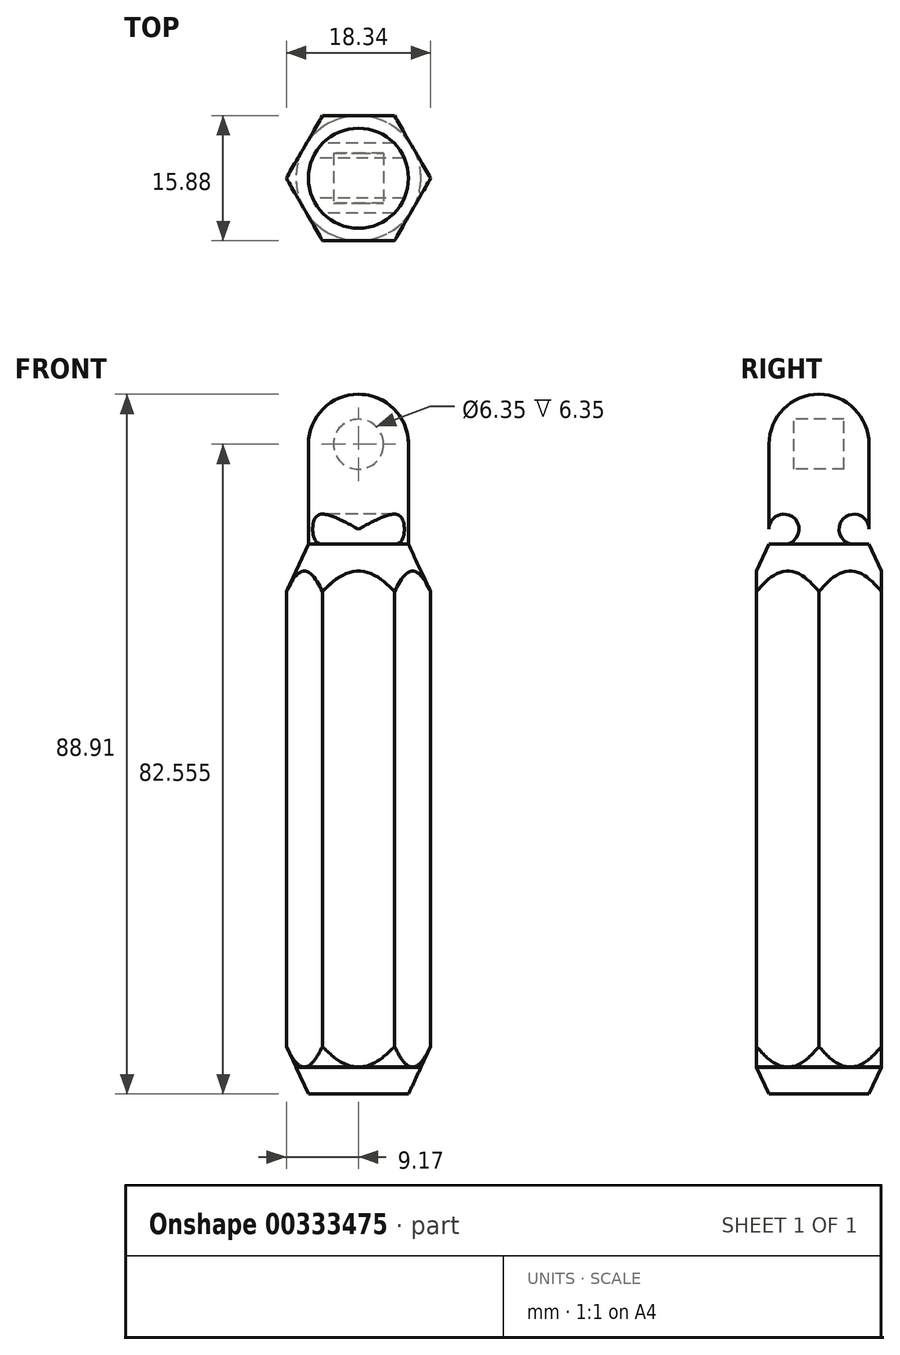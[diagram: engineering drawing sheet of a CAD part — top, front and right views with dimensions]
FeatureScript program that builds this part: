
annotation { "Feature Type Name" : "Feature", "Feature Type Description" : "" }
export const myFeature = defineFeature(function(context is Context, id is Id, definition is map)
    precondition{}
    {
        {
            var Q0;
            Q0=qCreatedBy(makeId("Front.planeOp"),FACE);
            var sketch = newSketch(context, id + "F0", { "sketchPlane" : qUnion([Q0])});
            skLineSegment(sketch, "E0.bottom", {"start": v(6.35, -34.93) * mm, "end": v(-6.35, -34.93) * mm});
            skLineSegment(sketch, "E0.top", {"start": v(6.35, 34.93) * mm, "end": v(-6.35, 34.93) * mm});
            skLineSegment(sketch, "E0.left", {"start": v(7.94, -31.52) * mm, "end": v(7.94, 31.52) * mm});
            skLineSegment(sketch, "E0.right", {"start": v(-7.94, -31.52) * mm, "end": v(-7.94, 31.52) * mm});
            skPoint(sketch, "E0.middle", {"position": v(0, 0) * mm});
            skLineSegment(sketch, "E1.left", {"start": v(6.35, 34.93) * mm, "end": v(6.35, 47.63) * mm});
            skLineSegment(sketch, "E1.right", {"start": v(-6.35, 34.93) * mm, "end": v(-6.35, 47.63) * mm});
            skArc(sketch, "E2", {"start": v(6.35, 47.63) * mm, "mid": v(0, 53.98) * mm, "end": v(-6.35, 47.63) * mm});
            skCircle(sketch, "E3", {"center": v(0, 47.63) * mm, "radius": 3.18 * mm});
            skLineSegment(sketch, "E4", {"start": v(-6.35, 34.92) * mm, "end": v(-7.94, 31.52) * mm});
            skLineSegment(sketch, "E5", {"start": v(6.35, 34.92) * mm, "end": v(7.94, 31.52) * mm});
            skPoint(sketch, "E6.orphan", {"position": v(-7.94, 34.93) * mm});
            skPoint(sketch, "E7.orphan", {"position": v(7.94, 34.93) * mm});
            skPoint(sketch, "E8.orphan", {"position": v(-6.35, 53.98) * mm});
            skPoint(sketch, "E9.orphan", {"position": v(6.35, 53.98) * mm});
            skLineSegment(sketch, "E10", {"start": v(-7.94, -31.52) * mm, "end": v(-6.35, -34.93) * mm});
            skLineSegment(sketch, "E11", {"start": v(7.94, -31.52) * mm, "end": v(6.35, -34.93) * mm});
            skPoint(sketch, "E12.orphan", {"position": v(-7.94, -34.93) * mm});
            skPoint(sketch, "E13.orphan", {"position": v(7.94, -34.93) * mm});
            skLineSegment(sketch, "E14", {"start": v(-7.94, 31.52) * mm, "end": v(7.94, 31.52) * mm});
            skLineSegment(sketch, "E15", {"start": v(0, -34.93) * mm, "end": v(0, 53.98) * mm});
            skLineSegment(sketch, "E16", {"start": v(-6.35, 34.93) * mm, "end": v(-6.35, 31.52) * mm});
            skLineSegment(sketch, "E17", {"start": v(6.35, 34.93) * mm, "end": v(6.35, 31.52) * mm});
            skLineSegment(sketch, "E18", {"start": v(-6.35, 34.93) * mm, "end": v(-12.7, 34.93) * mm});
            skLineSegment(sketch, "E19", {"start": v(-12.7, 34.92) * mm, "end": v(-12.7, 21.3) * mm});
            skLineSegment(sketch, "E20", {"start": v(-12.7, 21.3) * mm, "end": v(-6.35, 34.93) * mm});
            skLineSegment(sketch, "E21", {"start": v(6.35, 34.93) * mm, "end": v(12.7, 34.93) * mm});
            skLineSegment(sketch, "E22", {"start": v(12.7, 34.92) * mm, "end": v(12.7, 21.3) * mm});
            skLineSegment(sketch, "E23", {"start": v(12.7, 21.3) * mm, "end": v(6.35, 34.93) * mm});
            skLineSegment(sketch, "E24", {"start": v(12.7, -21.25) * mm, "end": v(6.35, -34.93) * mm});
            skPoint(sketch, "E25.orphan", {"position": v(-12.7, -34.93) * mm});
            skPoint(sketch, "E26.start.orphan", {"position": v(12.7, -34.91) * mm});
            skLineSegment(sketch, "E27", {"start": v(-6.35, -34.93) * mm, "end": v(-12.7, -21.3) * mm});
            skLineSegment(sketch, "E28", {"start": v(-12.7, -21.3) * mm, "end": v(-12.7, -34.93) * mm});
            skLineSegment(sketch, "E29", {"start": v(-12.7, -34.93) * mm, "end": v(-6.35, -34.93) * mm});
            skLineSegment(sketch, "E30", {"start": v(6.35, -34.93) * mm, "end": v(12.7, -34.91) * mm});
            skLineSegment(sketch, "E31", {"start": v(12.7, -21.25) * mm, "end": v(12.7, -34.91) * mm});
            skSolve(sketch);
        }
        {
            var Q0;
            {var subQ1=sQuery(id+"F0.wireOp",EDGE,"E1.left");Q0=makeQuery(id+"F0.imprint","IMPRINT",FACE,{"disambiguationData":[TD([[makeQuery(id+"F0.imprint","IMPRINT",EDGE,{"derivedFrom":subQ1}),1.0]])]});}
            var Q1;
            {var subQ0=sQuery(id+"F0.wireOp",EDGE,"E15");var subQ1=sQuery(id+"F0.wireOp",EDGE,"E3");var subQ2=makeQuery(id+"F0.imprint","INTERSECT",VERTEX,{"disambiguationData":[OD(0.0)],"derivedFrom":[subQ1,subQ0]});Q1=makeQuery(id+"F0.imprint","IMPRINT",FACE,{"disambiguationData":[TD([[makeQuery(id+"F0.imprint","IMPRINT",EDGE,{"disambiguationData":[TD([[subQ2,-1.0]])],"derivedFrom":subQ1}),1.0]])]});}
            var Q2;
            Q2=sQuery(id+"F0.wireOp",EDGE,"E15");
            revolve(context, id + "F1", {"entities" : qUnion([Q0, Q1]), "axis" : qUnion([Q2]), "revolveType" : RevolveType.FULL});
        }
        {
            var Q0;
            Q0=qCreatedBy(makeId("Top.planeOp"),FACE);
            var sketch = newSketch(context, id + "F2", { "sketchPlane" : qUnion([Q0])});
            skCircle(sketch, "E32.cCircle", {"center": v(0, 0) * mm, "radius": 7.94 * mm, "construction": true});
            skLineSegment(sketch, "E32.0", {"start": v(-4.58, 7.94) * mm, "end": v(4.58, 7.94) * mm});
            skLineSegment(sketch, "E32.1", {"start": v(4.58, 7.94) * mm, "end": v(9.17, 0) * mm});
            skLineSegment(sketch, "E32.2", {"start": v(9.17, 0) * mm, "end": v(4.58, -7.94) * mm});
            skLineSegment(sketch, "E32.3", {"start": v(4.58, -7.94) * mm, "end": v(-4.58, -7.94) * mm});
            skLineSegment(sketch, "E32.4", {"start": v(-4.58, -7.94) * mm, "end": v(-9.17, 0) * mm});
            skLineSegment(sketch, "E32.5", {"start": v(-9.17, 0) * mm, "end": v(-4.58, 7.94) * mm});
            skPoint(sketch, "E32.0.midPoint", {"position": v(0, 7.94) * mm});
            skSolve(sketch);
        }
        {
            var Q0;
            Q0=makeQuery(id+"F2.imprint","IMPRINT",FACE,{"disambiguationData":[TD([[makeQuery(id+"F2.imprint","IMPRINT",EDGE,{"derivedFrom":sQuery(id+"F2.wireOp",EDGE,"E32.0")}),-1.0]])]});
            extrude(context, id + "F3", {"entities" : qUnion([Q0]), "depth" : 69.85 * mm, "symmetric" : true});
        }
        {
            var Q0;
            {var subQ0=sQuery(id+"F0.wireOp",EDGE,"E21");Q0=makeQuery(id+"F0.imprint","IMPRINT",FACE,{"disambiguationData":[TD([[makeQuery(id+"F0.imprint","IMPRINT",EDGE,{"derivedFrom":subQ0}),-1.0]])]});}
            var Q1;
            {var subQ4=sQuery(id+"F0.wireOp",EDGE,"E11");Q1=makeQuery(id+"F0.imprint","IMPRINT",FACE,{"disambiguationData":[TD([[makeQuery(id+"F0.imprint","IMPRINT",EDGE,{"derivedFrom":subQ4}),1.0]])]});}
            var Q2;
            Q2=sQuery(id+"F0.wireOp",EDGE,"E15");
            revolve(context, id + "F4", {"operationType" : NewBodyOperationType.REMOVE, "entities" : qUnion([Q0, Q1]), "axis" : qUnion([Q2]), "revolveType" : RevolveType.FULL, "oppositeDirection" : true});
        }
        {
            var Q0;
            Q0=qCreatedBy(makeId("Right.planeOp"),FACE);
            var sketch = newSketch(context, id + "F5", { "sketchPlane" : qUnion([Q0])});
            skCircle(sketch, "E33", {"center": v(4.44, 36.83) * mm, "radius": 1.9 * mm});
            skCircle(sketch, "E34", {"center": v(-4.45, 36.83) * mm, "radius": 1.9 * mm});
            skLineSegment(sketch, "E35.bottom", {"start": v(6.35, 53.98) * mm, "end": v(-6.35, 53.98) * mm});
            skLineSegment(sketch, "E35.top", {"start": v(6.35, 34.93) * mm, "end": v(-6.35, 34.93) * mm});
            skLineSegment(sketch, "E35.left", {"start": v(6.35, 53.98) * mm, "end": v(6.35, 34.93) * mm});
            skLineSegment(sketch, "E35.right", {"start": v(-6.35, 53.98) * mm, "end": v(-6.35, 34.93) * mm});
            skPoint(sketch, "E35.middle", {"position": v(0, 44.45) * mm});
            skLineSegment(sketch, "E36.bottom", {"start": v(-6.35, 53.98) * mm, "end": v(-2.54, 53.98) * mm});
            skLineSegment(sketch, "E36.top", {"start": v(-6.35, 36.83) * mm, "end": v(-2.54, 36.83) * mm});
            skLineSegment(sketch, "E36.left", {"start": v(-6.35, 53.98) * mm, "end": v(-6.35, 36.83) * mm});
            skLineSegment(sketch, "E36.right", {"start": v(-2.54, 53.98) * mm, "end": v(-2.54, 36.83) * mm});
            skLineSegment(sketch, "E37.bottom", {"start": v(6.35, 53.98) * mm, "end": v(2.54, 53.98) * mm});
            skLineSegment(sketch, "E37.top", {"start": v(6.35, 36.83) * mm, "end": v(2.54, 36.83) * mm});
            skLineSegment(sketch, "E37.left", {"start": v(6.35, 53.98) * mm, "end": v(6.35, 36.83) * mm});
            skLineSegment(sketch, "E37.right", {"start": v(2.54, 53.98) * mm, "end": v(2.54, 36.83) * mm});
            skSolve(sketch);
        }
        {
            var Q0;
            Q0=makeQuery(id+"F5.imprint","IMPRINT",FACE,{"disambiguationData":[TD([[makeQuery(id+"F5.imprint","IMPRINT",EDGE,{"derivedFrom":sQuery(id+"F5.wireOp",EDGE,"E37.bottom")}),1.0]])]});
            var Q1;
            {var subQ0=sQuery(id+"F5.wireOp",EDGE,"E37.top");Q1=makeQuery(id+"F5.imprint","IMPRINT",FACE,{"disambiguationData":[TD([[makeQuery(id+"F5.imprint","IMPRINT",EDGE,{"derivedFrom":subQ0}),-1.0]])]});}
            var Q2;
            {var subQ0=sQuery(id+"F5.wireOp",EDGE,"E37.top");Q2=makeQuery(id+"F5.imprint","IMPRINT",FACE,{"disambiguationData":[TD([[makeQuery(id+"F5.imprint","IMPRINT",EDGE,{"derivedFrom":subQ0}),1.0]])]});}
            var Q3;
            {var subQ0=sQuery(id+"F5.wireOp",EDGE,"E35.left");Q3=makeQuery(id+"F5.imprint","IMPRINT",FACE,{"disambiguationData":[TD([[makeQuery(id+"F5.imprint","IMPRINT",EDGE,{"derivedFrom":subQ0}),-1.0]])]});}
            var Q4;
            {var subQ0=sQuery(id+"F5.wireOp",EDGE,"E35.right");Q4=makeQuery(id+"F5.imprint","IMPRINT",FACE,{"disambiguationData":[TD([[makeQuery(id+"F5.imprint","IMPRINT",EDGE,{"derivedFrom":subQ0}),1.0]])]});}
            var Q5;
            {var subQ0=sQuery(id+"F5.wireOp",EDGE,"E36.top");Q5=makeQuery(id+"F5.imprint","IMPRINT",FACE,{"disambiguationData":[TD([[makeQuery(id+"F5.imprint","IMPRINT",EDGE,{"derivedFrom":subQ0}),-1.0]])]});}
            var Q6;
            {var subQ0=sQuery(id+"F5.wireOp",EDGE,"E36.top");Q6=makeQuery(id+"F5.imprint","IMPRINT",FACE,{"disambiguationData":[TD([[makeQuery(id+"F5.imprint","IMPRINT",EDGE,{"derivedFrom":subQ0}),1.0]])]});}
            var Q7;
            Q7=makeQuery(id+"F5.imprint","IMPRINT",FACE,{"disambiguationData":[TD([[makeQuery(id+"F5.imprint","IMPRINT",EDGE,{"derivedFrom":sQuery(id+"F5.wireOp",EDGE,"E36.bottom")}),-1.0]])]});
            extrude(context, id + "F6", {"entities" : qUnion([Q0, Q1, Q2, Q3, Q4, Q5, Q6, Q7]), "operationType" : NewBodyOperationType.REMOVE, "depth" : 12.7 * mm, "symmetric" : true});
        }
        {
            var Q0;
            {var subQ0=sQuery(id+"F0.wireOp",EDGE,"E15");var subQ1=sQuery(id+"F0.wireOp",EDGE,"E3");var subQ2=makeQuery(id+"F0.imprint","INTERSECT",VERTEX,{"disambiguationData":[OD(0.0)],"derivedFrom":[subQ1,subQ0]});Q0=makeQuery(id+"F0.imprint","IMPRINT",FACE,{"disambiguationData":[TD([[makeQuery(id+"F0.imprint","IMPRINT",EDGE,{"disambiguationData":[TD([[subQ2,1.0]])],"derivedFrom":subQ1}),1.0]])]});}
            var Q1;
            {var subQ0=sQuery(id+"F0.wireOp",EDGE,"E15");var subQ1=sQuery(id+"F0.wireOp",EDGE,"E3");var subQ2=makeQuery(id+"F0.imprint","INTERSECT",VERTEX,{"disambiguationData":[OD(0.0)],"derivedFrom":[subQ1,subQ0]});Q1=makeQuery(id+"F0.imprint","IMPRINT",FACE,{"disambiguationData":[TD([[makeQuery(id+"F0.imprint","IMPRINT",EDGE,{"disambiguationData":[TD([[subQ2,-1.0]])],"derivedFrom":subQ1}),1.0]])]});}
            extrude(context, id + "F7", {"entities" : qUnion([Q0, Q1]), "operationType" : NewBodyOperationType.REMOVE, "oppositeDirection" : true, "depth" : 6.35 * mm, "symmetric" : true});
        }
    });
